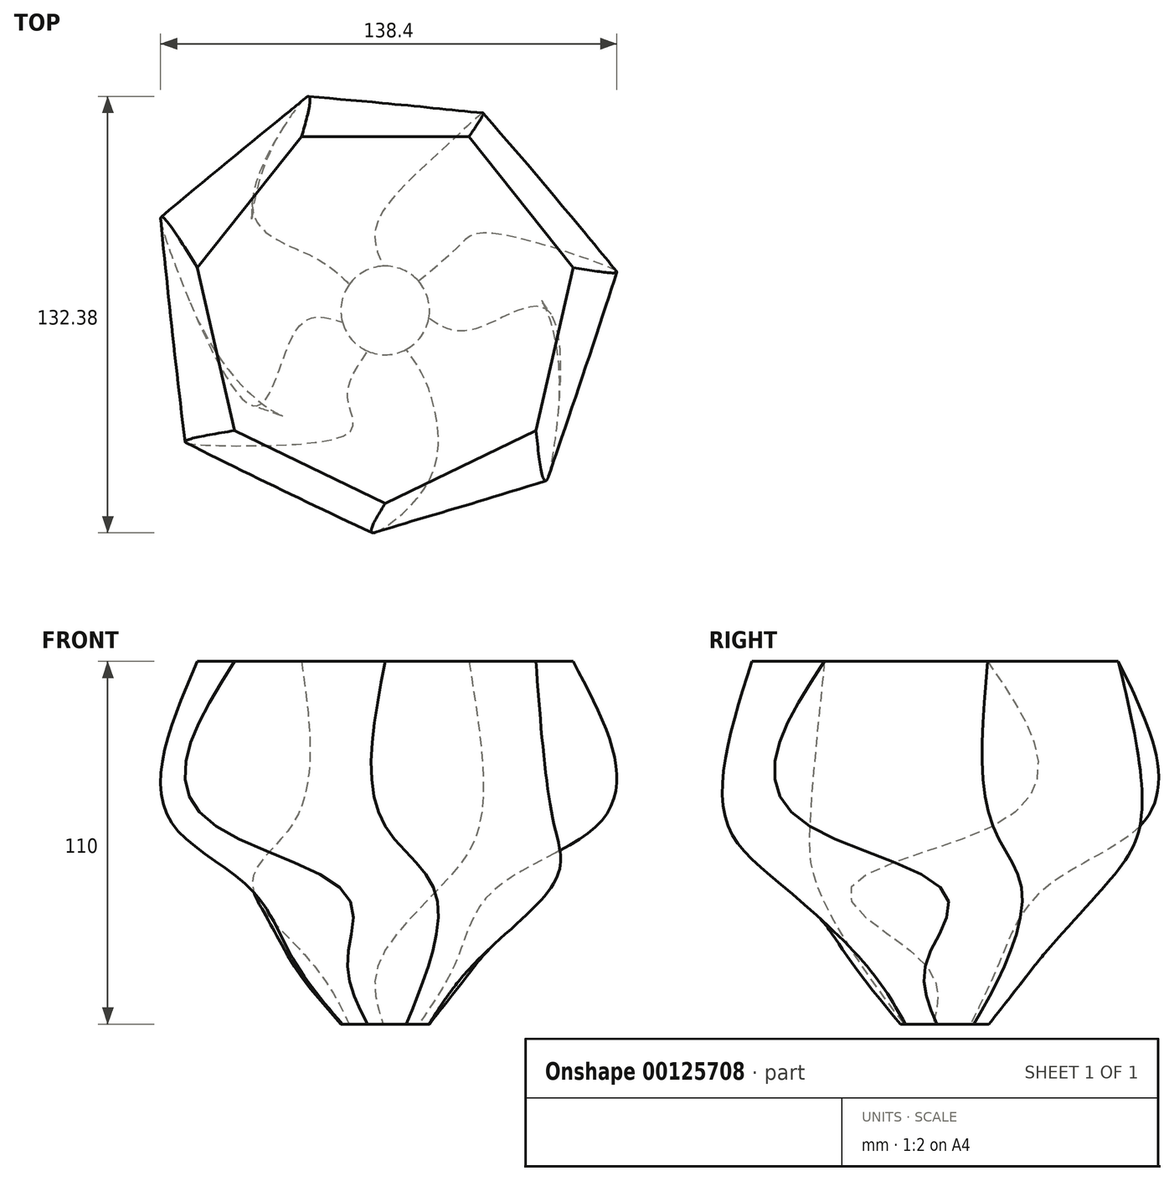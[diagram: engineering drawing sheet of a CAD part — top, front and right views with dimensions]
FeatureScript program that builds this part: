
annotation { "Feature Type Name" : "Feature", "Feature Type Description" : "" }
export const myFeature = defineFeature(function(context is Context, id is Id, definition is map)
    precondition{}
    {
        {
            var Q0;
            Q0=qCreatedBy(makeId("Top.planeOp"),FACE);
            cPlane(context, id + "F0", {"entities" : qUnion([Q0]), "cplaneType" : CPlaneType.OFFSET, "offset" : 20 * mm, "width" : 150 * mm, "height" : 150 * mm});
        }
        {
            var Q0;
            Q0=qCreatedBy(id+"F0.planeOp",FACE);
            cPlane(context, id + "F1", {"entities" : qUnion([Q0]), "cplaneType" : CPlaneType.OFFSET, "offset" : 20 * mm, "width" : 150 * mm, "height" : 150 * mm});
        }
        {
            var Q0;
            Q0=qCreatedBy(id+"F1.planeOp",FACE);
            cPlane(context, id + "F2", {"entities" : qUnion([Q0]), "cplaneType" : CPlaneType.OFFSET, "offset" : 20 * mm, "width" : 150 * mm, "height" : 150 * mm});
        }
        {
            var Q0;
            Q0=qCreatedBy(id+"F2.planeOp",FACE);
            cPlane(context, id + "F3", {"entities" : qUnion([Q0]), "cplaneType" : CPlaneType.OFFSET, "offset" : 50 * mm, "width" : 150 * mm, "height" : 150 * mm});
        }
        {
            var Q0;
            Q0=qCreatedBy(id+"F3.planeOp",FACE);
            var sketch = newSketch(context, id + "F4", { "sketchPlane" : qUnion([Q0])});
            skCircle(sketch, "E0.cCircle", {"center": v(0, 0) * mm, "radius": 52.69 * mm, "construction": true});
            skLineSegment(sketch, "E0.0", {"start": v(-25.37, 52.69) * mm, "end": v(25.37, 52.69) * mm});
            skLineSegment(sketch, "E0.1", {"start": v(25.37, 52.69) * mm, "end": v(57.01, 13.01) * mm});
            skLineSegment(sketch, "E0.2", {"start": v(57.01, 13.01) * mm, "end": v(45.72, -36.46) * mm});
            skLineSegment(sketch, "E0.3", {"start": v(45.72, -36.46) * mm, "end": v(0, -58.48) * mm});
            skLineSegment(sketch, "E0.4", {"start": v(0, -58.48) * mm, "end": v(-45.72, -36.46) * mm});
            skLineSegment(sketch, "E0.5", {"start": v(-45.72, -36.46) * mm, "end": v(-57.01, 13.01) * mm});
            skLineSegment(sketch, "E0.6", {"start": v(-57.01, 13.01) * mm, "end": v(-25.37, 52.69) * mm});
            skPoint(sketch, "E0.0.midPoint", {"position": v(0, 52.69) * mm});
            skSolve(sketch);
        }
        {
            var Q0;
            Q0=qCreatedBy(id+"F2.planeOp",FACE);
            var sketch = newSketch(context, id + "F5", { "sketchPlane" : qUnion([Q0])});
            skCircle(sketch, "E1.cCircle", {"center": v(0, 0) * mm, "radius": 59.19 * mm, "construction": true});
            skLineSegment(sketch, "E1.0", {"start": v(-28.5, 59.19) * mm, "end": v(28.5, 59.19) * mm});
            skLineSegment(sketch, "E1.1", {"start": v(28.5, 59.19) * mm, "end": v(64.04, 14.62) * mm});
            skLineSegment(sketch, "E1.2", {"start": v(64.04, 14.62) * mm, "end": v(51.36, -40.96) * mm});
            skLineSegment(sketch, "E1.3", {"start": v(51.36, -40.96) * mm, "end": v(0, -65.7) * mm});
            skLineSegment(sketch, "E1.4", {"start": v(0, -65.7) * mm, "end": v(-51.36, -40.96) * mm});
            skLineSegment(sketch, "E1.5", {"start": v(-51.36, -40.96) * mm, "end": v(-64.04, 14.62) * mm});
            skLineSegment(sketch, "E1.6", {"start": v(-64.04, 14.62) * mm, "end": v(-28.5, 59.19) * mm});
            skPoint(sketch, "E1.0.midPoint", {"position": v(0, 59.19) * mm});
            skSolve(sketch);
        }
        {
            var Q0;
            Q0=qCreatedBy(id+"F1.planeOp",FACE);
            var sketch = newSketch(context, id + "F6", { "sketchPlane" : qUnion([Q0])});
            skCircle(sketch, "E2.cCircle", {"center": v(0, 0) * mm, "radius": 39.9 * mm, "construction": true});
            skLineSegment(sketch, "E2.0", {"start": v(-39.9, -28.98) * mm, "end": v(-39.9, 28.98) * mm});
            skLineSegment(sketch, "E2.1", {"start": v(-39.9, 28.98) * mm, "end": v(15.24, 46.9) * mm});
            skLineSegment(sketch, "E2.2", {"start": v(15.24, 46.9) * mm, "end": v(49.31, 0) * mm});
            skLineSegment(sketch, "E2.3", {"start": v(49.31, 0) * mm, "end": v(15.24, -46.9) * mm});
            skLineSegment(sketch, "E2.4", {"start": v(15.24, -46.9) * mm, "end": v(-39.9, -28.98) * mm});
            skPoint(sketch, "E2.0.midPoint", {"position": v(-39.9, 0) * mm});
            skSolve(sketch);
        }
        {
            var Q0;
            Q0=qCreatedBy(id+"F0.planeOp",FACE);
            var sketch = newSketch(context, id + "F7", { "sketchPlane" : qUnion([Q0])});
            skCircle(sketch, "E3", {"center": v(0, 0) * mm, "radius": 29.12 * mm});
            skSolve(sketch);
        }
        {
            var Q0;
            Q0=qCreatedBy(makeId("Top.planeOp"),FACE);
            var sketch = newSketch(context, id + "F8", { "sketchPlane" : qUnion([Q0])});
            skCircle(sketch, "E4", {"center": v(0, 0) * mm, "radius": 13.45 * mm});
            skSolve(sketch);
        }
        {
            var Q0;
            Q0=makeQuery(id+"F4.imprint","IMPRINT",FACE,{"disambiguationData":[TD([[makeQuery(id+"F4.imprint","IMPRINT",EDGE,{"derivedFrom":sQuery(id+"F4.wireOp",EDGE,"E0.0")}),-1.0]])]});
            var Q1;
            Q1=makeQuery(id+"F5.imprint","IMPRINT",FACE,{"disambiguationData":[TD([[makeQuery(id+"F5.imprint","IMPRINT",EDGE,{"derivedFrom":sQuery(id+"F5.wireOp",EDGE,"E1.0")}),-1.0]])]});
            var Q2;
            Q2=makeQuery(id+"F6.imprint","IMPRINT",FACE,{"disambiguationData":[TD([[makeQuery(id+"F6.imprint","IMPRINT",EDGE,{"derivedFrom":sQuery(id+"F6.wireOp",EDGE,"E2.0")}),-1.0]])]});
            var Q3;
            Q3=makeQuery(id+"F7.imprint","IMPRINT",FACE,{"disambiguationData":[TD([[makeQuery(id+"F7.imprint","IMPRINT",EDGE,{"derivedFrom":sQuery(id+"F7.wireOp",EDGE,"E3")}),1.0]])]});
            var Q4;
            Q4=makeQuery(id+"F8.imprint","IMPRINT",FACE,{"disambiguationData":[TD([[makeQuery(id+"F8.imprint","IMPRINT",EDGE,{"derivedFrom":sQuery(id+"F8.wireOp",EDGE,"E4")}),1.0]])]});
            loft(context, id + "F9", {"sheetProfilesArray" : [{ "sheetProfileEntities" : qUnion([Q0]) }, { "sheetProfileEntities" : qUnion([Q1]) }, { "sheetProfileEntities" : qUnion([Q2]) }, { "sheetProfileEntities" : qUnion([Q3]) }, { "sheetProfileEntities" : qUnion([Q4]) }]});
        }
    });
